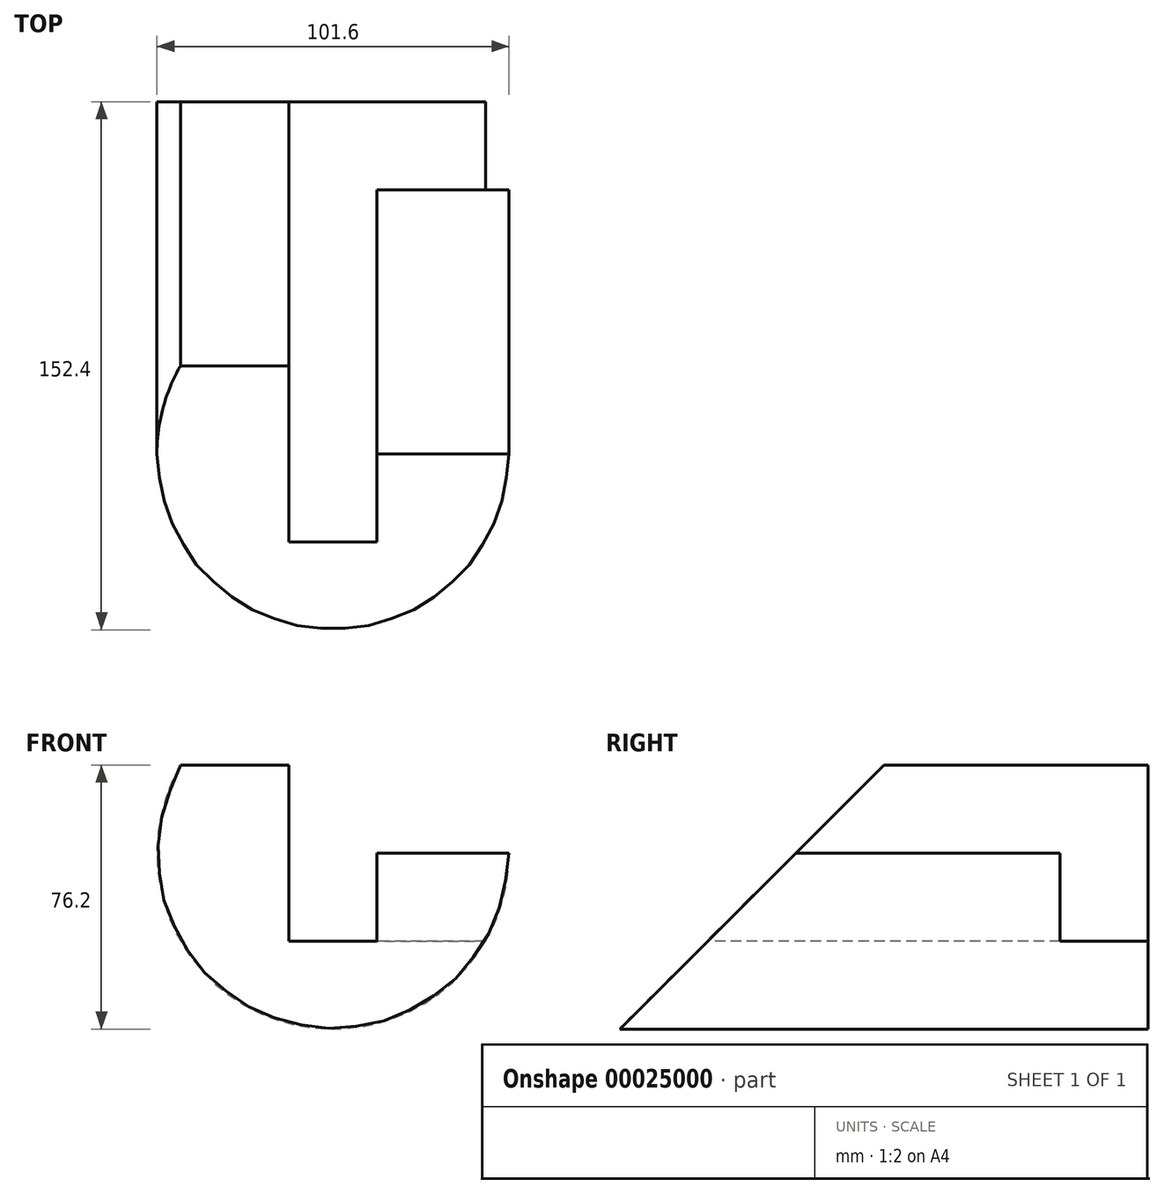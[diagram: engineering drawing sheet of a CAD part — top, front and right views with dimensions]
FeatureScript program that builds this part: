
annotation { "Feature Type Name" : "Feature", "Feature Type Description" : "" }
export const myFeature = defineFeature(function(context is Context, id is Id, definition is map)
    precondition{}
    {
        {
            var Q0;
            Q0=qCreatedBy(makeId("Front.planeOp"),FACE);
            var sketch = newSketch(context, id + "F0", { "sketchPlane" : qUnion([Q0])});
            skArc(sketch, "E0", {"start": v(-44, 25.4) * mm, "mid": v(-13.15, -49.07) * mm, "end": v(50.8, 0) * mm});
            skLineSegment(sketch, "E1.rect.bottom", {"start": v(-12.7, -25.4) * mm, "end": v(12.7, -25.4) * mm});
            skLineSegment(sketch, "E1.rect.top", {"start": v(-12.7, 25.4) * mm, "end": v(12.7, 25.4) * mm});
            skLineSegment(sketch, "E1.rect.left", {"start": v(-12.7, -25.4) * mm, "end": v(-12.7, 25.4) * mm});
            skLineSegment(sketch, "E1.rect.right", {"start": v(12.7, -25.4) * mm, "end": v(12.7, 25.4) * mm});
            skLineSegment(sketch, "E2", {"start": v(-12.7, 25.4) * mm, "end": v(-44, 25.4) * mm});
            skLineSegment(sketch, "E3", {"start": v(12.7, 0) * mm, "end": v(50.8, 0) * mm});
            skSolve(sketch);
        }
        {
            var Q0;
            Q0=makeQuery(id+"F0.imprint","IMPRINT",FACE,{"disambiguationData":[TD([[makeQuery(id+"F0.imprint","IMPRINT",EDGE,{"derivedFrom":sQuery(id+"F0.wireOp",EDGE,"E0")}),1.0]])]});
            extrude(context, id + "F1", {"entities" : qUnion([Q0]), "oppositeDirection" : true, "depth" : 152.4 * mm});
        }
        {
            var Q0;
            Q0=qCreatedBy(makeId("Right.planeOp"),FACE);
            var sketch = newSketch(context, id + "F2", { "sketchPlane" : qUnion([Q0])});
            skLineSegment(sketch, "E4", {"start": v(0, -50.8) * mm, "end": v(76.2, 25.4) * mm});
            skLineSegment(sketch, "E5", {"start": v(76.2, 25.4) * mm, "end": v(0, 25.4) * mm});
            skLineSegment(sketch, "E6", {"start": v(0, 25.4) * mm, "end": v(0, -50.8) * mm});
            skLineSegment(sketch, "E7.bottom", {"start": v(152.4, 0) * mm, "end": v(127, 0) * mm});
            skLineSegment(sketch, "E7.top", {"start": v(152.4, -25.4) * mm, "end": v(127, -25.4) * mm});
            skLineSegment(sketch, "E7.left", {"start": v(152.4, 0) * mm, "end": v(152.4, -25.4) * mm});
            skLineSegment(sketch, "E7.right", {"start": v(127, 0) * mm, "end": v(127, -25.4) * mm});
            skSolve(sketch);
        }
        {
            var Q0;
            Q0=makeQuery(id+"F2.imprint","IMPRINT",FACE,{"disambiguationData":[TD([[makeQuery(id+"F2.imprint","IMPRINT",EDGE,{"derivedFrom":sQuery(id+"F2.wireOp",EDGE,"E4")}),1.0]])]});
            extrude(context, id + "F3", {"entities" : qUnion([Q0]), "operationType" : NewBodyOperationType.REMOVE, "endBound" : BoundingType.THROUGH_ALL, "oppositeDirection" : true, "depth" : 25.4 * mm});
        }
        {
            var Q0;
            Q0=makeQuery(id+"F2.imprint","IMPRINT",FACE,{"disambiguationData":[TD([[makeQuery(id+"F2.imprint","IMPRINT",EDGE,{"derivedFrom":sQuery(id+"F2.wireOp",EDGE,"E4")}),1.0]])]});
            var Q1;
            Q1=makeQuery(id+"F2.imprint","IMPRINT",FACE,{"disambiguationData":[TD([[makeQuery(id+"F2.imprint","IMPRINT",EDGE,{"derivedFrom":sQuery(id+"F2.wireOp",EDGE,"E7.bottom")}),1.0]])]});
            extrude(context, id + "F4", {"entities" : qUnion([Q0, Q1]), "operationType" : NewBodyOperationType.REMOVE, "endBound" : BoundingType.THROUGH_ALL, "depth" : 25.4 * mm});
        }
    });
